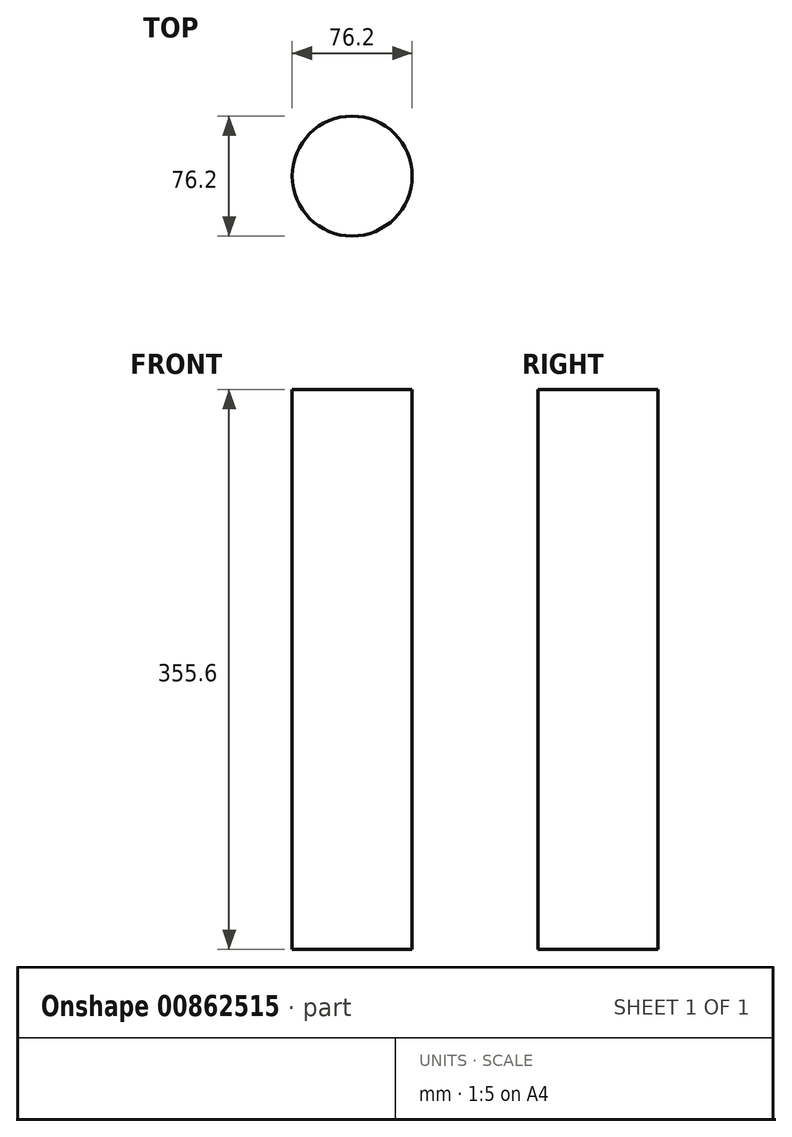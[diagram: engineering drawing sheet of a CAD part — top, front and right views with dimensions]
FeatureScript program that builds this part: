
annotation { "Feature Type Name" : "Feature", "Feature Type Description" : "" }
export const myFeature = defineFeature(function(context is Context, id is Id, definition is map)
    precondition{}
    {
        {
            var Q0;
            Q0=qCreatedBy(makeId("Top.planeOp"),FACE);
            var sketch = newSketch(context, id + "F0", { "sketchPlane" : qUnion([Q0])});
            skCircle(sketch, "E0", {"center": v(0, 0) * mm, "radius": 38.1 * mm});
            skSolve(sketch);
        }
        {
            var Q0;
            Q0 = qSketchRegion(id + "F0", true);
            extrude(context, id + "F1", {"entities" : qUnion([Q0]), "depth" : 355.6 * mm, "offsetDistance" : 25.4 * mm});
        }
    });
